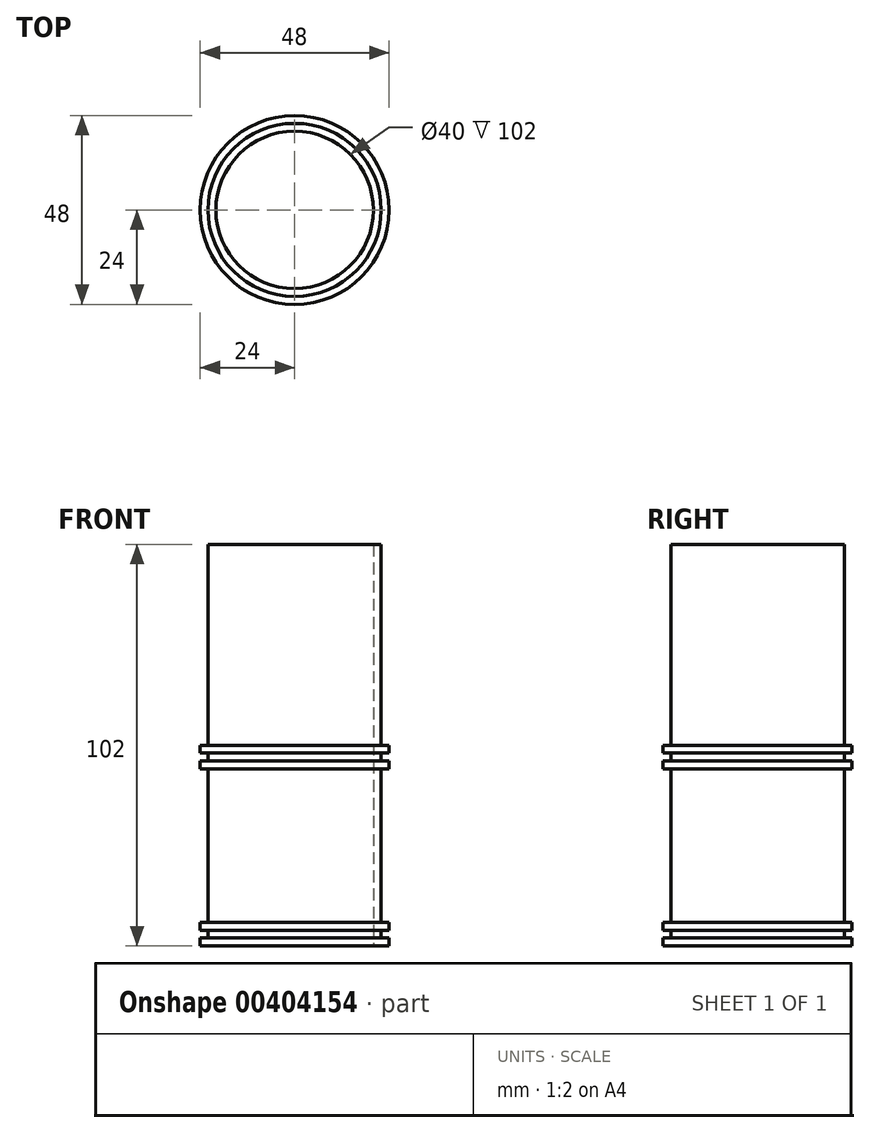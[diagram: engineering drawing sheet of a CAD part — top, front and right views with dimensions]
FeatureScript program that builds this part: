
annotation { "Feature Type Name" : "Feature", "Feature Type Description" : "" }
export const myFeature = defineFeature(function(context is Context, id is Id, definition is map)
    precondition{}
    {
        {
            var Q0;
            Q0=qCreatedBy(makeId("Top.planeOp"),FACE);
            var sketch = newSketch(context, id + "F0", { "sketchPlane" : qUnion([Q0])});
            skCircle(sketch, "E0", {"center": v(0, 0) * mm, "radius": 20 * mm});
            skCircle(sketch, "E1", {"center": v(0, 0) * mm, "radius": 22 * mm});
            skCircle(sketch, "E2", {"center": v(0, 0) * mm, "radius": 24 * mm});
            skSolve(sketch);
        }
        {
            var Q0;
            Q0=makeQuery(id+"F0.imprint","IMPRINT",FACE,{"disambiguationData":[TD([[makeQuery(id+"F0.imprint","IMPRINT",EDGE,{"derivedFrom":sQuery(id+"F0.wireOp",EDGE,"E0")}),-1.0]])]});
            extrude(context, id + "F1", {"entities" : qUnion([Q0]), "depth" : 100 * mm, "hasSecondDirection" : true, "secondDirectionOppositeDirection" : true, "secondDirectionDepth" : 2 * mm});
        }
        {
            var Q0;
            Q0=makeQuery(id+"F0.imprint","IMPRINT",FACE,{"disambiguationData":[TD([[makeQuery(id+"F0.imprint","IMPRINT",EDGE,{"derivedFrom":sQuery(id+"F0.wireOp",EDGE,"E1")}),-1.0]])]});
            extrude(context, id + "F2", {"entities" : qUnion([Q0]), "operationType" : NewBodyOperationType.ADD, "oppositeDirection" : true, "depth" : 2 * mm});
        }
        {
            var Q0;
            Q0=makeQuery(id+"F0.imprint","IMPRINT",FACE,{"disambiguationData":[TD([[makeQuery(id+"F0.imprint","IMPRINT",EDGE,{"derivedFrom":sQuery(id+"F0.wireOp",EDGE,"E1")}),-1.0]])]});
            extrude(context, id + "F3", {"entities" : qUnion([Q0]), "operationType" : NewBodyOperationType.ADD, "depth" : 4 * mm, "hasSecondDirection" : true, "secondDirectionOppositeDirection" : false, "secondDirectionDepth" : 2 * mm});
        }
        {
            var Q0;
            Q0=makeQuery(id+"F0.imprint","IMPRINT",FACE,{"disambiguationData":[TD([[makeQuery(id+"F0.imprint","IMPRINT",EDGE,{"derivedFrom":sQuery(id+"F0.wireOp",EDGE,"E1")}),-1.0]])]});
            extrude(context, id + "F4", {"entities" : qUnion([Q0]), "operationType" : NewBodyOperationType.ADD, "depth" : 45 * mm, "hasSecondDirection" : true, "secondDirectionOppositeDirection" : false, "secondDirectionDepth" : 43 * mm});
        }
        {
            var Q0;
            Q0=makeQuery(id+"F0.imprint","IMPRINT",FACE,{"disambiguationData":[TD([[makeQuery(id+"F0.imprint","IMPRINT",EDGE,{"derivedFrom":sQuery(id+"F0.wireOp",EDGE,"E1")}),-1.0]])]});
            extrude(context, id + "F5", {"entities" : qUnion([Q0]), "operationType" : NewBodyOperationType.ADD, "depth" : 49 * mm, "hasSecondDirection" : true, "secondDirectionOppositeDirection" : false, "secondDirectionDepth" : 47 * mm});
        }
    });
